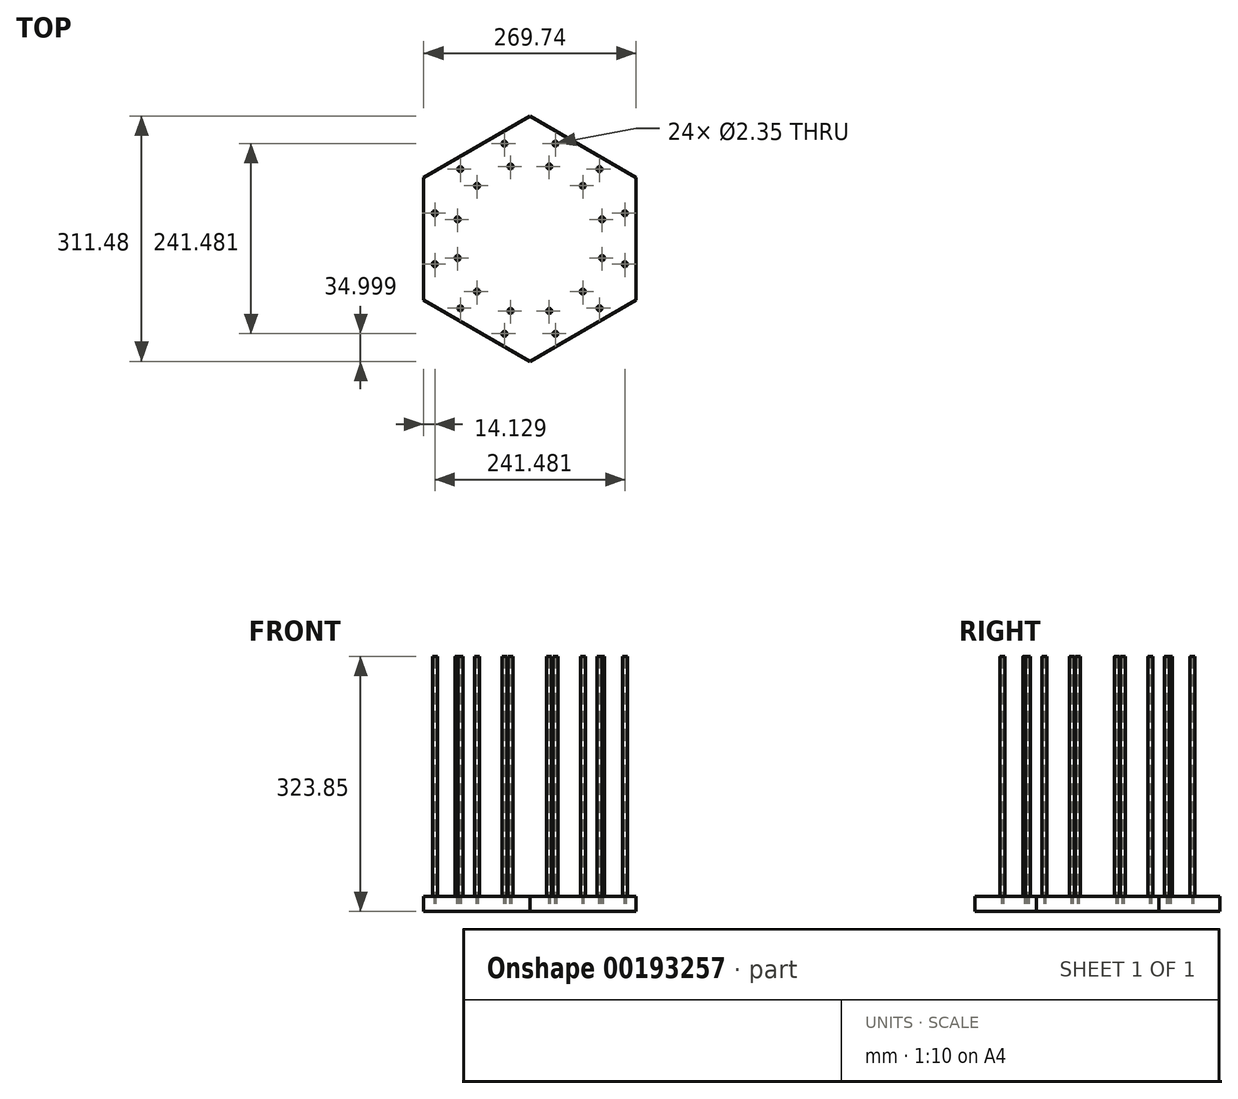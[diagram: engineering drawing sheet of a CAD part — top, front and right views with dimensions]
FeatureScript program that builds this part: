
annotation { "Feature Type Name" : "Feature", "Feature Type Description" : "" }
export const myFeature = defineFeature(function(context is Context, id is Id, definition is map)
    precondition{}
    {
        {
            var Q0;
            Q0=qCreatedBy(makeId("Top.planeOp"),FACE);
            var sketch = newSketch(context, id + "F0", { "sketchPlane" : qUnion([Q0])});
            skCircle(sketch, "E0.cCircle", {"center": v(0, 0) * mm, "radius": 155.74 * mm, "construction": true});
            skLineSegment(sketch, "E0.0", {"start": v(0, 155.74) * mm, "end": v(134.87, 77.87) * mm});
            skLineSegment(sketch, "E0.1", {"start": v(134.87, 77.87) * mm, "end": v(134.87, -77.87) * mm});
            skLineSegment(sketch, "E0.2", {"start": v(134.87, -77.87) * mm, "end": v(0, -155.74) * mm});
            skLineSegment(sketch, "E0.3", {"start": v(0, -155.74) * mm, "end": v(-134.87, -77.87) * mm});
            skLineSegment(sketch, "E0.4", {"start": v(-134.87, -77.87) * mm, "end": v(-134.87, 77.87) * mm});
            skLineSegment(sketch, "E0.5", {"start": v(-134.87, 77.87) * mm, "end": v(0, 155.74) * mm});
            skSolve(sketch);
        }
        {
            var Q0;
            Q0 = qSketchRegion(id + "F0", true);
            extrude(context, id + "F1", {"entities" : qUnion([Q0]), "depth" : 19.05 * mm});
        }
        {
            var Q0;
            Q0=makeQuery(id+"F1.opExtrude","CAP_FACE",FACE,{"disambiguationData":[OSD([sQuery(id+"F0.wireOp",EDGE,"E0.0"),sQuery(id+"F0.wireOp",EDGE,"E0.1"),sQuery(id+"F0.wireOp",EDGE,"E0.2"),sQuery(id+"F0.wireOp",EDGE,"E0.3"),sQuery(id+"F0.wireOp",EDGE,"E0.4"),sQuery(id+"F0.wireOp",EDGE,"E0.5")])],"isStart":false});
            var sketch = newSketch(context, id + "F2", { "sketchPlane" : qUnion([Q0])});
            skLineSegment(sketch, "E1", {"start": v(0, 0) * mm, "end": v(0, 155.74) * mm});
            skLineSegment(sketch, "E2", {"start": v(0, 0) * mm, "end": v(24.59, 91.76) * mm});
            skCircle(sketch, "E3", {"center": v(24.59, 91.76) * mm, "radius": 3.17 * mm});
            skLineSegment(sketch, "E4", {"start": v(24.59, 91.76) * mm, "end": v(32.35, 120.74) * mm});
            skCircle(sketch, "E5", {"center": v(32.35, 120.74) * mm, "radius": 3.17 * mm});
            skCircle(sketch, "E6.1.0", {"center": v(-24.59, 91.76) * mm, "radius": 3.17 * mm});
            skCircle(sketch, "E6.1.1", {"center": v(-32.35, 120.74) * mm, "radius": 3.17 * mm});
            skCircle(sketch, "E6.2.0", {"center": v(-67.18, 67.18) * mm, "radius": 3.17 * mm});
            skCircle(sketch, "E6.2.1", {"center": v(-88.39, 88.39) * mm, "radius": 3.17 * mm});
            skCircle(sketch, "E6.3.0", {"center": v(-91.76, 24.59) * mm, "radius": 3.17 * mm});
            skCircle(sketch, "E6.3.1", {"center": v(-120.74, 32.35) * mm, "radius": 3.17 * mm});
            skCircle(sketch, "E6.4.0", {"center": v(-91.76, -24.59) * mm, "radius": 3.17 * mm});
            skCircle(sketch, "E6.4.1", {"center": v(-120.74, -32.35) * mm, "radius": 3.17 * mm});
            skCircle(sketch, "E6.5.0", {"center": v(-67.18, -67.18) * mm, "radius": 3.17 * mm});
            skCircle(sketch, "E6.5.1", {"center": v(-88.39, -88.39) * mm, "radius": 3.17 * mm});
            skCircle(sketch, "E6.6.0", {"center": v(-24.59, -91.76) * mm, "radius": 3.17 * mm});
            skCircle(sketch, "E6.6.1", {"center": v(-32.35, -120.74) * mm, "radius": 3.17 * mm});
            skCircle(sketch, "E6.7.0", {"center": v(24.59, -91.76) * mm, "radius": 3.17 * mm});
            skCircle(sketch, "E6.7.1", {"center": v(32.35, -120.74) * mm, "radius": 3.17 * mm});
            skCircle(sketch, "E6.8.0", {"center": v(67.18, -67.18) * mm, "radius": 3.17 * mm});
            skCircle(sketch, "E6.8.1", {"center": v(88.39, -88.39) * mm, "radius": 3.17 * mm});
            skCircle(sketch, "E6.9.0", {"center": v(91.76, -24.59) * mm, "radius": 3.17 * mm});
            skCircle(sketch, "E6.9.1", {"center": v(120.74, -32.35) * mm, "radius": 3.17 * mm});
            skCircle(sketch, "E6.10.0", {"center": v(91.76, 24.59) * mm, "radius": 3.17 * mm});
            skCircle(sketch, "E6.10.1", {"center": v(120.74, 32.35) * mm, "radius": 3.17 * mm});
            skCircle(sketch, "E6.11.0", {"center": v(67.18, 67.18) * mm, "radius": 3.17 * mm});
            skCircle(sketch, "E6.11.1", {"center": v(88.39, 88.39) * mm, "radius": 3.17 * mm});
            skPoint(sketch, "E6.center", {"position": v(0, 0) * mm});
            skSolve(sketch);
        }
        {
            var Q0;
            Q0 = qSketchRegion(id + "F2", true);
            extrude(context, id + "F3", {"entities" : qUnion([Q0]), "operationType" : NewBodyOperationType.REMOVE, "oppositeDirection" : true, "depth" : 19.05 * mm});
        }
        {
            var Q0;
            Q0=makeQuery(id+"F1.opExtrude","CAP_FACE",FACE,{"disambiguationData":[OSD([sQuery(id+"F0.wireOp",EDGE,"E0.0"),sQuery(id+"F0.wireOp",EDGE,"E0.1"),sQuery(id+"F0.wireOp",EDGE,"E0.2"),sQuery(id+"F0.wireOp",EDGE,"E0.3"),sQuery(id+"F0.wireOp",EDGE,"E0.4"),sQuery(id+"F0.wireOp",EDGE,"E0.5")])],"isStart":false});
            var sketch = newSketch(context, id + "F4", { "sketchPlane" : qUnion([Q0])});
            skCircle(sketch, "E7", {"center": v(-88.39, 88.39) * mm, "radius": 3.17 * mm});
            skCircle(sketch, "E8", {"center": v(-67.18, 67.18) * mm, "radius": 3.17 * mm});
            skCircle(sketch, "E9", {"center": v(-88.39, 88.39) * mm, "radius": 1.17 * mm});
            skCircle(sketch, "E10", {"center": v(-67.18, 67.18) * mm, "radius": 1.17 * mm});
            skCircle(sketch, "E11.1.0", {"center": v(-120.74, 32.35) * mm, "radius": 3.17 * mm});
            skCircle(sketch, "E11.1.1", {"center": v(-91.76, 24.59) * mm, "radius": 1.17 * mm});
            skCircle(sketch, "E11.1.2", {"center": v(-120.74, 32.35) * mm, "radius": 1.17 * mm});
            skCircle(sketch, "E11.1.3", {"center": v(-91.76, 24.59) * mm, "radius": 3.17 * mm});
            skCircle(sketch, "E11.2.0", {"center": v(-120.74, -32.35) * mm, "radius": 3.17 * mm});
            skCircle(sketch, "E11.2.1", {"center": v(-91.76, -24.59) * mm, "radius": 1.17 * mm});
            skCircle(sketch, "E11.2.2", {"center": v(-120.74, -32.35) * mm, "radius": 1.17 * mm});
            skCircle(sketch, "E11.2.3", {"center": v(-91.76, -24.59) * mm, "radius": 3.17 * mm});
            skCircle(sketch, "E11.3.0", {"center": v(-88.39, -88.39) * mm, "radius": 3.17 * mm});
            skCircle(sketch, "E11.3.1", {"center": v(-67.18, -67.18) * mm, "radius": 1.17 * mm});
            skCircle(sketch, "E11.3.2", {"center": v(-88.39, -88.39) * mm, "radius": 1.17 * mm});
            skCircle(sketch, "E11.3.3", {"center": v(-67.18, -67.18) * mm, "radius": 3.17 * mm});
            skCircle(sketch, "E11.4.0", {"center": v(-32.35, -120.74) * mm, "radius": 3.17 * mm});
            skCircle(sketch, "E11.4.1", {"center": v(-24.59, -91.76) * mm, "radius": 1.17 * mm});
            skCircle(sketch, "E11.4.2", {"center": v(-32.35, -120.74) * mm, "radius": 1.17 * mm});
            skCircle(sketch, "E11.4.3", {"center": v(-24.59, -91.76) * mm, "radius": 3.17 * mm});
            skCircle(sketch, "E11.5.0", {"center": v(32.35, -120.74) * mm, "radius": 3.17 * mm});
            skCircle(sketch, "E11.5.1", {"center": v(24.59, -91.76) * mm, "radius": 1.17 * mm});
            skCircle(sketch, "E11.5.2", {"center": v(32.35, -120.74) * mm, "radius": 1.17 * mm});
            skCircle(sketch, "E11.5.3", {"center": v(24.59, -91.76) * mm, "radius": 3.17 * mm});
            skCircle(sketch, "E11.6.0", {"center": v(88.39, -88.39) * mm, "radius": 3.17 * mm});
            skCircle(sketch, "E11.6.1", {"center": v(67.18, -67.18) * mm, "radius": 1.17 * mm});
            skCircle(sketch, "E11.6.2", {"center": v(88.39, -88.39) * mm, "radius": 1.17 * mm});
            skCircle(sketch, "E11.6.3", {"center": v(67.18, -67.18) * mm, "radius": 3.17 * mm});
            skCircle(sketch, "E11.7.0", {"center": v(120.74, -32.35) * mm, "radius": 3.17 * mm});
            skCircle(sketch, "E11.7.1", {"center": v(91.76, -24.59) * mm, "radius": 1.17 * mm});
            skCircle(sketch, "E11.7.2", {"center": v(120.74, -32.35) * mm, "radius": 1.17 * mm});
            skCircle(sketch, "E11.7.3", {"center": v(91.76, -24.59) * mm, "radius": 3.17 * mm});
            skCircle(sketch, "E11.8.0", {"center": v(120.74, 32.35) * mm, "radius": 3.17 * mm});
            skCircle(sketch, "E11.8.1", {"center": v(91.76, 24.59) * mm, "radius": 1.17 * mm});
            skCircle(sketch, "E11.8.2", {"center": v(120.74, 32.35) * mm, "radius": 1.17 * mm});
            skCircle(sketch, "E11.8.3", {"center": v(91.76, 24.59) * mm, "radius": 3.17 * mm});
            skCircle(sketch, "E11.9.0", {"center": v(88.39, 88.39) * mm, "radius": 3.17 * mm});
            skCircle(sketch, "E11.9.1", {"center": v(67.18, 67.18) * mm, "radius": 1.17 * mm});
            skCircle(sketch, "E11.9.2", {"center": v(88.39, 88.39) * mm, "radius": 1.17 * mm});
            skCircle(sketch, "E11.9.3", {"center": v(67.18, 67.18) * mm, "radius": 3.17 * mm});
            skCircle(sketch, "E11.10.0", {"center": v(32.35, 120.74) * mm, "radius": 3.17 * mm});
            skCircle(sketch, "E11.10.1", {"center": v(24.59, 91.76) * mm, "radius": 1.17 * mm});
            skCircle(sketch, "E11.10.2", {"center": v(32.35, 120.74) * mm, "radius": 1.17 * mm});
            skCircle(sketch, "E11.10.3", {"center": v(24.59, 91.76) * mm, "radius": 3.17 * mm});
            skCircle(sketch, "E11.11.0", {"center": v(-32.35, 120.74) * mm, "radius": 3.17 * mm});
            skCircle(sketch, "E11.11.1", {"center": v(-24.59, 91.76) * mm, "radius": 1.17 * mm});
            skCircle(sketch, "E11.11.2", {"center": v(-32.35, 120.74) * mm, "radius": 1.17 * mm});
            skCircle(sketch, "E11.11.3", {"center": v(-24.59, 91.76) * mm, "radius": 3.17 * mm});
            skPoint(sketch, "E11.center", {"position": v(0, 0) * mm});
            skSolve(sketch);
        }
        {
            var Q0;
            Q0 = qSketchRegion(id + "F4", true);
            extrude(context, id + "F5", {"entities" : qUnion([Q0]), "operationType" : NewBodyOperationType.ADD, "depth" : 304.8 * mm, "hasSecondDirection" : true, "secondDirectionOppositeDirection" : true, "secondDirectionDepth" : 19.05 * mm});
        }
    });
